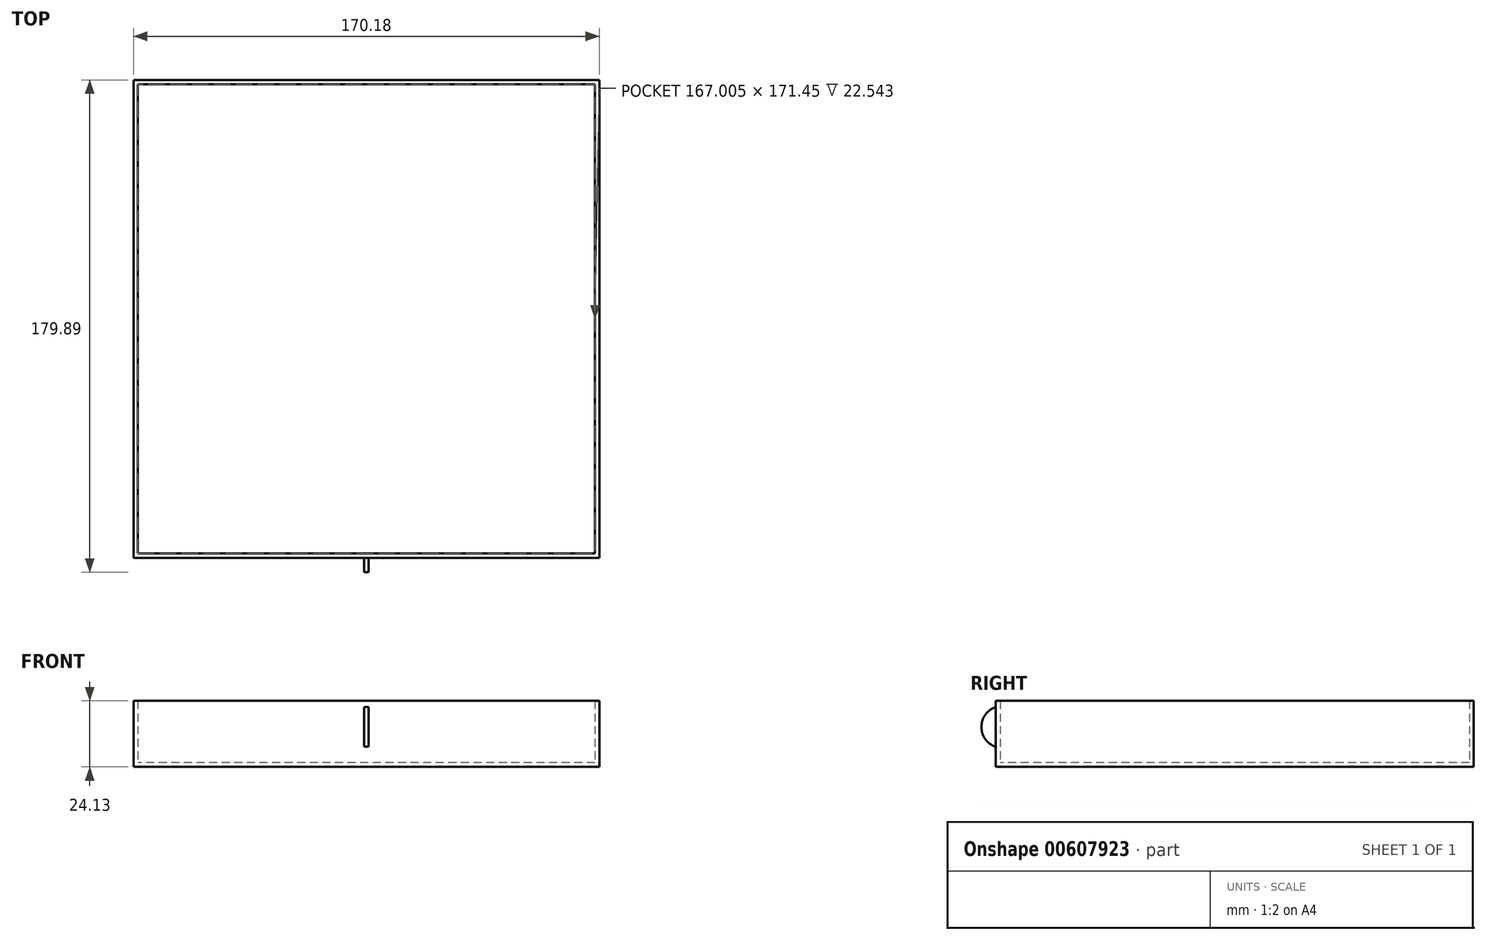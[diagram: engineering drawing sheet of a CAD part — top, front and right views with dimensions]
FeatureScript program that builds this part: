
annotation { "Feature Type Name" : "Feature", "Feature Type Description" : "" }
export const myFeature = defineFeature(function(context is Context, id is Id, definition is map)
    precondition{}
    {
        {
            var Q0;
            Q0=qCreatedBy(makeId("Top.planeOp"),FACE);
            var sketch = newSketch(context, id + "F0", { "sketchPlane" : qUnion([Q0])});
            skLineSegment(sketch, "E0.bottom", {"start": v(-85.1, 87.31) * mm, "end": v(85.1, 87.31) * mm});
            skLineSegment(sketch, "E0.top", {"start": v(-85.1, -87.31) * mm, "end": v(85.1, -87.31) * mm});
            skLineSegment(sketch, "E0.left", {"start": v(-85.1, 87.31) * mm, "end": v(-85.1, -87.31) * mm});
            skLineSegment(sketch, "E0.right", {"start": v(85.1, 87.31) * mm, "end": v(85.1, -87.31) * mm});
            skSolve(sketch);
        }
        {
            var Q0;
            Q0 = qSketchRegion(id + "F0", true);
            extrude(context, id + "F1", {"entities" : qUnion([Q0]), "depth" : 1.59 * mm, "offsetDistance" : 25.4 * mm});
        }
        {
            var Q0;
            Q0=makeQuery(id+"F1.opExtrude","CAP_FACE",FACE,{"disambiguationData":[OSD([sQuery(id+"F0.wireOp",EDGE,"E0.bottom"),sQuery(id+"F0.wireOp",EDGE,"E0.top"),sQuery(id+"F0.wireOp",EDGE,"E0.left"),sQuery(id+"F0.wireOp",EDGE,"E0.right")])],"isStart":false});
            var sketch = newSketch(context, id + "F2", { "sketchPlane" : qUnion([Q0])});
            skLineSegment(sketch, "E1.0", {"start": v(-83.5, 85.73) * mm, "end": v(-83.5, -85.73) * mm});
            skLineSegment(sketch, "E1.1", {"start": v(83.5, 85.73) * mm, "end": v(-83.5, 85.73) * mm});
            skLineSegment(sketch, "E1.2", {"start": v(83.5, -85.73) * mm, "end": v(83.5, 85.73) * mm});
            skLineSegment(sketch, "E1.3", {"start": v(-83.5, -85.73) * mm, "end": v(83.5, -85.73) * mm});
            skLineSegment(sketch, "E2.0", {"start": v(-85.1, 87.31) * mm, "end": v(-85.1, -87.31) * mm});
            skLineSegment(sketch, "E2.1", {"start": v(-85.1, -87.31) * mm, "end": v(85.1, -87.31) * mm});
            skLineSegment(sketch, "E2.2", {"start": v(85.1, 87.31) * mm, "end": v(85.1, -87.31) * mm});
            skLineSegment(sketch, "E2.3", {"start": v(-85.1, 87.31) * mm, "end": v(85.1, 87.31) * mm});
            skSolve(sketch);
        }
        {
            var Q0;
            Q0 = qSketchRegion(id + "F2", true);
            extrude(context, id + "F3", {"entities" : qUnion([Q0]), "operationType" : NewBodyOperationType.ADD, "depth" : 22.54 * mm, "offsetDistance" : 25.4 * mm});
        }
        {
            var Q0;
            Q0=qCreatedBy(makeId("Right.planeOp"),FACE);
            var sketch = newSketch(context, id + "F4", { "sketchPlane" : qUnion([Q0])});
            skArc(sketch, "E3", {"start": v(-87.31, 21.85) * mm, "mid": v(-92.58, 14.6) * mm, "end": v(-87.31, 7.36) * mm});
            skLineSegment(sketch, "E4", {"start": v(-87.31, 21.85) * mm, "end": v(-87.31, 7.36) * mm});
            skSolve(sketch);
        }
        {
            var Q0;
            Q0 = qSketchRegion(id + "F4", true);
            extrude(context, id + "F5", {"entities" : qUnion([Q0]), "operationType" : NewBodyOperationType.ADD, "endBound" : BoundingType.SYMMETRIC, "depth" : 1.59 * mm, "offsetDistance" : 25.4 * mm});
        }
    });
